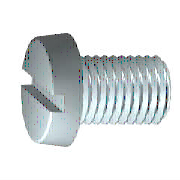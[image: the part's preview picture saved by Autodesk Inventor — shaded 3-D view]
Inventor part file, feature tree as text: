
AUTODESK INVENTOR PART (.ipt)
format: ipt  version: 2024.2 (Build 282272000, 272)  size: 190,976 bytes
history: native  units: mm (DEFAULTED — no unit token found)
features: extrude x1, plane x1
ambient origin geometry x7: Origin, YZ Plane, XZ Plane, X Axis, Y Axis, Z Axis, Center Point
bodies: Solid1 (feature_tree), Body (feature_tree)
feature tree (2):
  extrude  "Slot"  Depth=16.0mm
  plane  "Work Plane1"
